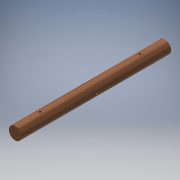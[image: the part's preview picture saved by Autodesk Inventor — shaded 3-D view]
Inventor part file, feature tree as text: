
AUTODESK INVENTOR PART (.ipt)
format: ipt  version: 2019.2 (Build 232265000, 265)  size: 127,488 bytes
history: native  units: in
note: dims shown in document units (in); Inventor stores cm internally (conversion verified against a paired STEP export)
features: sketch x3, extrude x2, plane x1, mirror x1, hole x1
ambient origin geometry x8: Origin, YZ Plane, XZ Plane, XY Plane, X Axis, Y Axis, Z Axis, Center Point
bodies: Solid1 (feature_tree)
feature tree (8):
  extrude  "Extrusion1"  Depth=72.0in TaperAngle=0.0deg
  plane  "Work Plane2"
  extrude  "Extrusion3"  Depth=2.0in
  mirror  "Mirror1"
  hole  "Hole2"  [1 undecoded]
  sketch  "Sketch1"  dims[d0=6.0in d1=72.0in d2=0.0in]
  sketch  "Sketch4"  dims[d16=3.0in d17=2.0in]
  sketch  "Sketch5"  dims[d19=12.0in d20=1.0in d21=0.0in d22=12.0in d23=12.0in d24=1.0in d25=0.75in d26=0.625in d27=0.19in d28=0.5635in d29=1.0in d30=0.8108in]
note: 1 required parameter value undecoded (feature->parameter linkage not recoverable at this tier; creation-order binding heuristic only, values carry confidence <= 0.55)
